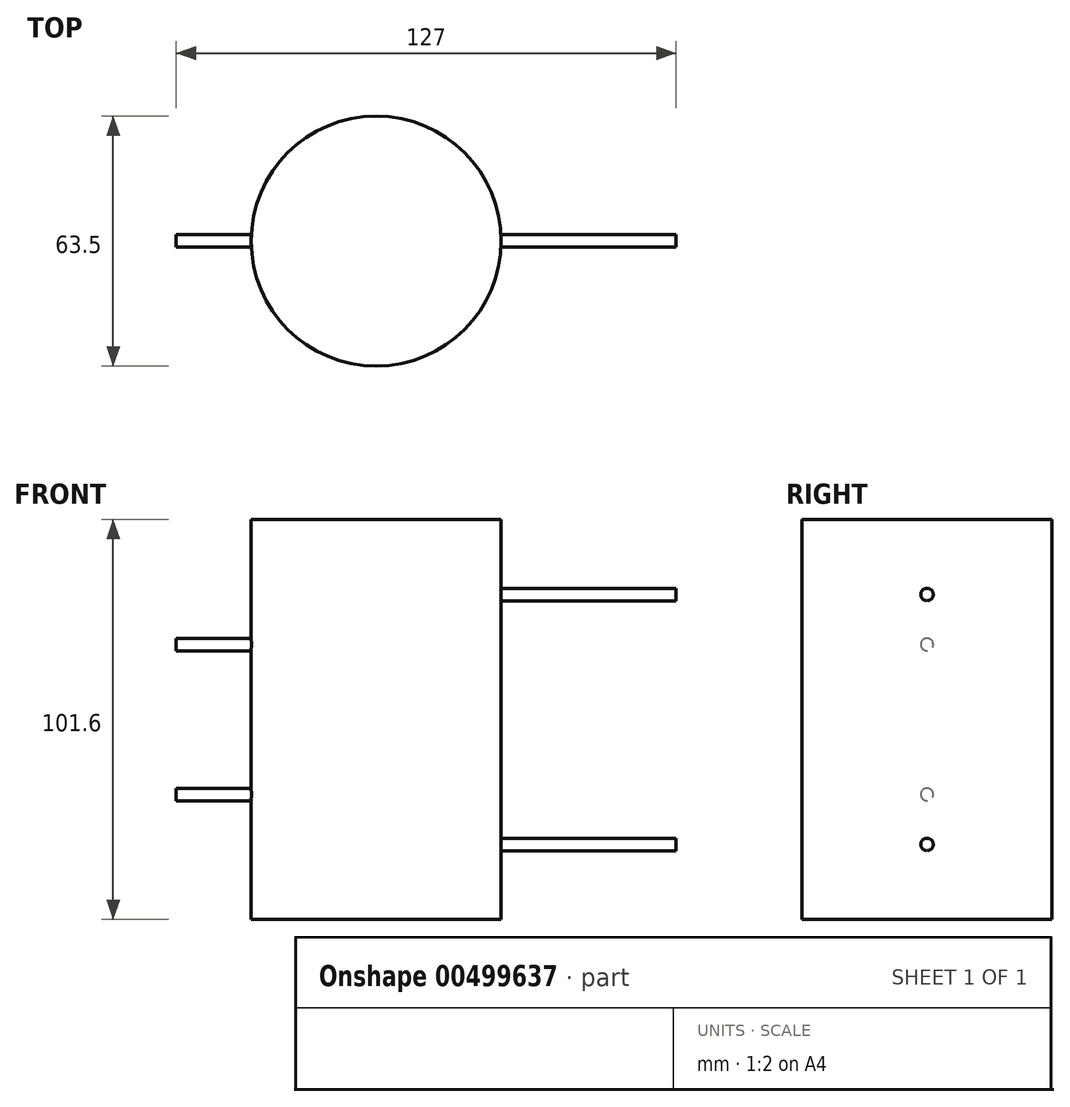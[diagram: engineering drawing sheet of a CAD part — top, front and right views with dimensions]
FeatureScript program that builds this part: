
annotation { "Feature Type Name" : "Feature", "Feature Type Description" : "" }
export const myFeature = defineFeature(function(context is Context, id is Id, definition is map)
    precondition{}
    {
        {
            var Q0;
            Q0=qCreatedBy(makeId("Top.planeOp"),FACE);
            var sketch = newSketch(context, id + "F0", { "sketchPlane" : qUnion([Q0])});
            skCircle(sketch, "E0", {"center": v(0, 0) * mm, "radius": 31.75 * mm});
            skSolve(sketch);
        }
        {
            var Q0;
            Q0 = qSketchRegion(id + "F0", true);
            extrude(context, id + "F1", {"entities" : qUnion([Q0]), "depth" : 50.8 * mm, "hasSecondDirection" : true, "secondDirectionOppositeDirection" : true, "secondDirectionDepth" : 50.8 * mm});
        }
        {
            var Q0;
            Q0=qCreatedBy(makeId("Right.planeOp"),FACE);
            var sketch = newSketch(context, id + "F2", { "sketchPlane" : qUnion([Q0])});
            skLineSegment(sketch, "E1", {"start": v(0, 0) * mm, "end": v(0, -31.75) * mm});
            skLineSegment(sketch, "E2", {"start": v(0, 0) * mm, "end": v(0, 31.75) * mm});
            skCircle(sketch, "E3", {"center": v(0, 31.75) * mm, "radius": 1.59 * mm});
            skCircle(sketch, "E4", {"center": v(0, -31.75) * mm, "radius": 1.59 * mm});
            skSolve(sketch);
        }
        {
            var Q0;
            Q0 = qSketchRegion(id + "F2", true);
            extrude(context, id + "F3", {"entities" : qUnion([Q0]), "operationType" : NewBodyOperationType.ADD, "depth" : 76.2 * mm});
        }
        {
            var Q0;
            Q0=qCreatedBy(makeId("Right.planeOp"),FACE);
            var sketch = newSketch(context, id + "F4", { "sketchPlane" : qUnion([Q0])});
            skLineSegment(sketch, "E5", {"start": v(0, 0) * mm, "end": v(0, 19.05) * mm});
            skLineSegment(sketch, "E6", {"start": v(0, 0) * mm, "end": v(0, -19.05) * mm});
            skCircle(sketch, "E7", {"center": v(0, 19.05) * mm, "radius": 1.59 * mm});
            skCircle(sketch, "E8", {"center": v(0, -19.05) * mm, "radius": 1.59 * mm});
            skSolve(sketch);
        }
        {
            var Q0;
            Q0 = qSketchRegion(id + "F4", true);
            extrude(context, id + "F5", {"entities" : qUnion([Q0]), "operationType" : NewBodyOperationType.ADD, "oppositeDirection" : true, "depth" : 50.8 * mm});
        }
    });
